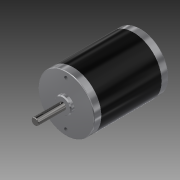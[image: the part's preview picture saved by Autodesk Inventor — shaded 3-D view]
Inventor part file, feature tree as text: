
AUTODESK INVENTOR PART (.ipt)
format: ipt  version: 2018 (Build 220112000, 112)  size: 168,960 bytes
history: native  units: in
note: dims shown in document units (in); Inventor stores cm internally (conversion verified against a paired STEP export)
features: thread x2, chamfer x1, other x1, imported_body x1
ambient origin geometry x8: Origin, YZ Plane, XZ Plane, XY Plane, X Axis, Y Axis, Z Axis, Center Point
bodies: Body1 (feature_tree)
feature tree (5):
  chamfer  "Chamfer3"  Distance=0.3937in
  other  "217-3371-STEP1"
  thread  "Thread1"  [1 undecoded]
  thread  "Thread2"  [1 undecoded]
  imported_body  "Base1"
note: 2 required parameter values undecoded (feature->parameter linkage not recoverable at this tier; creation-order binding heuristic only, values carry confidence <= 0.55)
